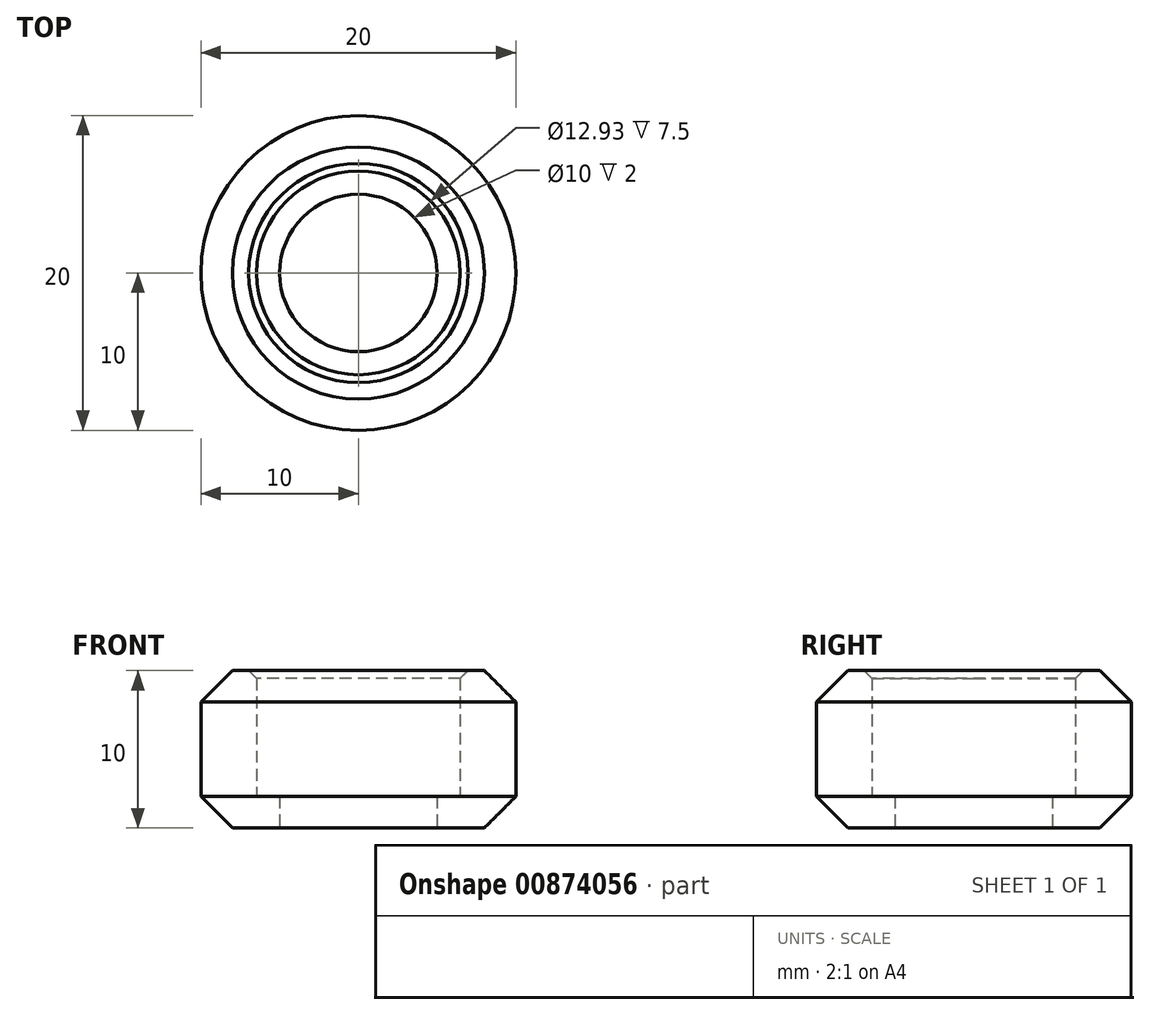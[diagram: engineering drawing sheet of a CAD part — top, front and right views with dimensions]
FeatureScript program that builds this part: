
annotation { "Feature Type Name" : "Feature", "Feature Type Description" : "" }
export const myFeature = defineFeature(function(context is Context, id is Id, definition is map)
    precondition{}
    {
        {
            var Q0;
            Q0=qCreatedBy(makeId("Top.planeOp"),FACE);
            var sketch = newSketch(context, id + "F0", { "sketchPlane" : qUnion([Q0])});
            skCircle(sketch, "E0", {"center": v(0, 0) * mm, "radius": 10 * mm});
            skSolve(sketch);
        }
        {
            var Q0;
            Q0=qCreatedBy(makeId("Top.planeOp"),FACE);
            var sketch = newSketch(context, id + "F1", { "sketchPlane" : qUnion([Q0])});
            skCircle(sketch, "E1", {"center": v(0, 0) * mm, "radius": 6.46 * mm});
            skSolve(sketch);
        }
        {
            var Q0;
            Q0=makeQuery(id+"F0.imprint","IMPRINT",FACE,{"disambiguationData":[TD([[makeQuery(id+"F0.imprint","IMPRINT",EDGE,{"derivedFrom":sQuery(id+"F0.wireOp",EDGE,"E0")}),1.0]])]});
            var Q1;
            Q1=sQuery(id+"F0.wireOp",EDGE,"E0");
            extrude(context, id + "F2", {"entities" : qUnion([Q0]), "surfaceEntities" : qUnion([Q1]), "depth" : 10 * mm, "offsetDistance" : 25.4 * mm});
        }
        {
            var Q0;
            Q0 = qSketchRegion(id + "F1", true);
            extrude(context, id + "F3", {"entities" : qUnion([Q0]), "operationType" : NewBodyOperationType.REMOVE, "depth" : 12 * mm, "offsetDistance" : 25.4 * mm});
        }
        {
            var Q0;
            Q0 = qSketchRegion(id + "F1", true);
            var sketch = newSketch(context, id + "F4", { "sketchPlane" : qUnion([Q0])});
            skSolve(sketch);
        }
        {
            var Q0;
            Q0=qCreatedBy(makeId("Top.planeOp"),FACE);
            var sketch = newSketch(context, id + "F5", { "sketchPlane" : qUnion([Q0])});
            skCircle(sketch, "E2", {"center": v(0, 0) * mm, "radius": 5 * mm});
            skSolve(sketch);
        }
        {
            var Q0;
            Q0=makeQuery(id+"F4.imprint","IMPRINT",FACE,{"disambiguationData":[TD([[makeQuery(id+"F4.imprint","IMPRINT",EDGE,{"derivedFrom":makeQuery(id+"F1.imprint","IMPRINT",EDGE,{"derivedFrom":sQuery(id+"F1.wireOp",EDGE,"E1")})}),1.0]])]});
            var Q1;
            Q1=sQuery(id+"F1.wireOp",EDGE,"E1");
            var Q2;
            Q2=sQuery(id+"F5.wireOp",EDGE,"E2");
            extrude(context, id + "F6", {"entities" : qUnion([Q0]), "operationType" : NewBodyOperationType.ADD, "surfaceEntities" : qUnion([Q1, Q2]), "depth" : 2 * mm, "offsetDistance" : 25 * mm});
        }
        {
            var Q0;
            Q0=sQuery(id+"F0.wireOp",VERTEX,"E0.center");
            var Q1;
            Q1=makeQuery(id+"F2.opExtrude","SWEPT_BODY",BODY,{"disambiguationData":[OSD([sQuery(id+"F0.wireOp",EDGE,"E0")])]});
            hole(context, id + "F7", {"style" : HoleStyle.SIMPLE, "endStyle" : HoleEndStyle.THROUGH, "oppositeDirection" : true, "holeDiameter" : 10 * mm, "majorDiameter" : 5 * mm, "isTappedThrough" : true, "tappedDepth" : 12 * mm, "tapClearance" : 3, "startFromSketch" : true, "locations" : qUnion([Q0]), "scope" : qUnion([Q1])});
        }
        {
            var Q0;
            Q0=makeQuery(id+"F2.opExtrude","CAP_EDGE",EDGE,{"disambiguationData":[OSD([sQuery(id+"F0.wireOp",EDGE,"E0")])],"isStart":false});
            var Q1;
            Q1=makeQuery(id+"F2.opExtrude","CAP_EDGE",EDGE,{"disambiguationData":[OSD([sQuery(id+"F0.wireOp",EDGE,"E0")])],"isStart":true});
            chamfer(context, id + "F8", {"entities" : qUnion([Q0, Q1]), "chamferType" : ChamferType.OFFSET_ANGLE, "width" : 2 * mm, "oppositeDirection" : false, "angle" : 45 * degree, "tangentPropagation" : true});
        }
        {
            var Q0;
            Q0=makeQuery(id+"F3.boolean.opBoolean","INTERSECT",EDGE,{"derivedFrom":[makeQuery(id+"F2.opExtrude","CAP_FACE",FACE,{"disambiguationData":[OSD([sQuery(id+"F0.wireOp",EDGE,"E0")])],"isStart":false}),makeQuery(id+"F3.opExtrude","SWEPT_FACE",FACE,{"disambiguationData":[OSD([sQuery(id+"F1.wireOp",EDGE,"E1")])]})]});
            chamfer(context, id + "F9", {"entities" : qUnion([Q0]), "chamferType" : ChamferType.OFFSET_ANGLE, "width" : 0.5 * mm, "oppositeDirection" : false, "angle" : 45 * degree, "tangentPropagation" : true});
        }
    });
